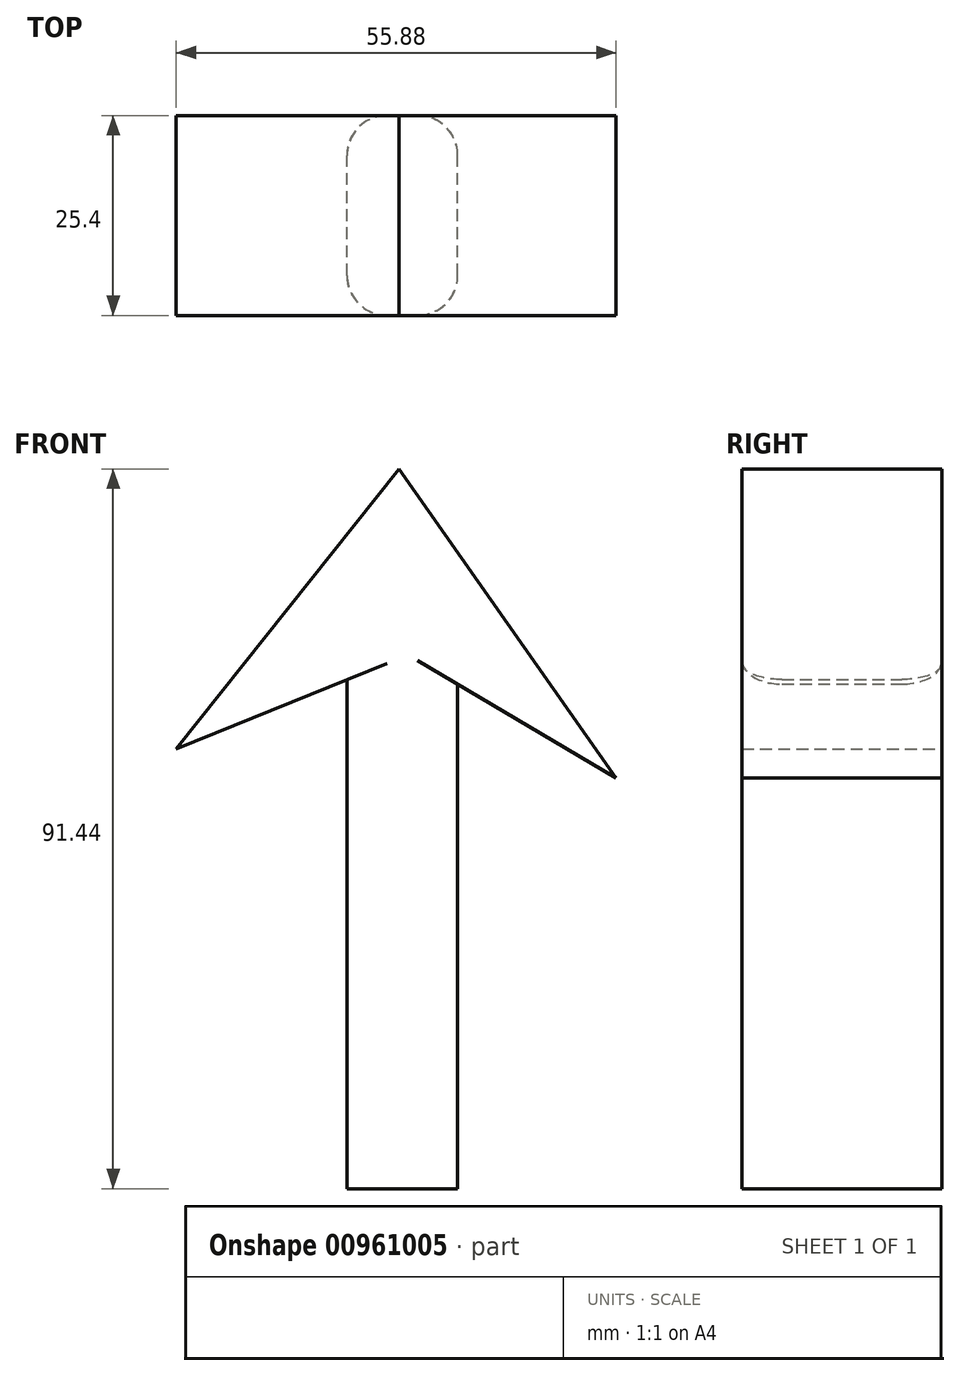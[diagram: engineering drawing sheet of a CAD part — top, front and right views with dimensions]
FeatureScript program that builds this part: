
annotation { "Feature Type Name" : "Feature", "Feature Type Description" : "" }
export const myFeature = defineFeature(function(context is Context, id is Id, definition is map)
    precondition{}
    {
        {
            var Q0;
            Q0=qCreatedBy(makeId("Front.planeOp"),FACE);
            var sketch = newSketch(context, id + "F0", { "sketchPlane" : qUnion([Q0])});
            skLineSegment(sketch, "E0", {"start": v(-10.65, 26.38) * mm, "end": v(-10.65, -38.3) * mm});
            skLineSegment(sketch, "E1", {"start": v(-10.65, -38.3) * mm, "end": v(3.42, -38.3) * mm});
            skLineSegment(sketch, "E2", {"start": v(3.42, -38.3) * mm, "end": v(3.42, 25.8) * mm});
            skLineSegment(sketch, "E3", {"start": v(3.42, 25.8) * mm, "end": v(23.54, 13.87) * mm});
            skLineSegment(sketch, "E4", {"start": v(23.54, 13.87) * mm, "end": v(-4, 53.14) * mm});
            skLineSegment(sketch, "E5", {"start": v(-4, 53.14) * mm, "end": v(-32.34, 17.58) * mm});
            skLineSegment(sketch, "E6", {"start": v(-32.34, 17.58) * mm, "end": v(-10.65, 26.38) * mm});
            skLineSegment(sketch, "E7", {"start": v(-5.96, -38.3) * mm, "end": v(-5.96, 50.7) * mm});
            skLineSegment(sketch, "E8", {"start": v(0, -38.3) * mm, "end": v(0, 47.43) * mm});
            skSolve(sketch);
        }
        {
            var Q0;
            Q0 = qSketchRegion(id + "F0", true);
            extrude(context, id + "F1", {"entities" : qUnion([Q0]), "depth" : 25.4 * mm, "offsetDistance" : 25.4 * mm});
        }
        {
            var Q0;
            Q0=makeQuery(id+"F1.opExtrude","CAP_EDGE",EDGE,{"disambiguationData":[OSD([sQuery(id+"F0.wireOp",EDGE,"E2")])],"isStart":false});
            var Q1;
            Q1=makeQuery(id+"F1.opExtrude","CAP_EDGE",EDGE,{"disambiguationData":[OSD([sQuery(id+"F0.wireOp",EDGE,"E0")])],"isStart":false});
            var Q2;
            Q2=makeQuery(id+"F1.opExtrude","CAP_EDGE",EDGE,{"disambiguationData":[OSD([sQuery(id+"F0.wireOp",EDGE,"E2")])],"isStart":true});
            var Q3;
            Q3=makeQuery(id+"F1.opExtrude","CAP_EDGE",EDGE,{"disambiguationData":[OSD([sQuery(id+"F0.wireOp",EDGE,"E0")])],"isStart":true});
            fillet(context, id + "F2", {"entities" : qUnion([Q0, Q1, Q2, Q3]), "radius" : 5.08 * mm, "tangentPropagation" : true, "allowEdgeOverflow" : false});
        }
    });
